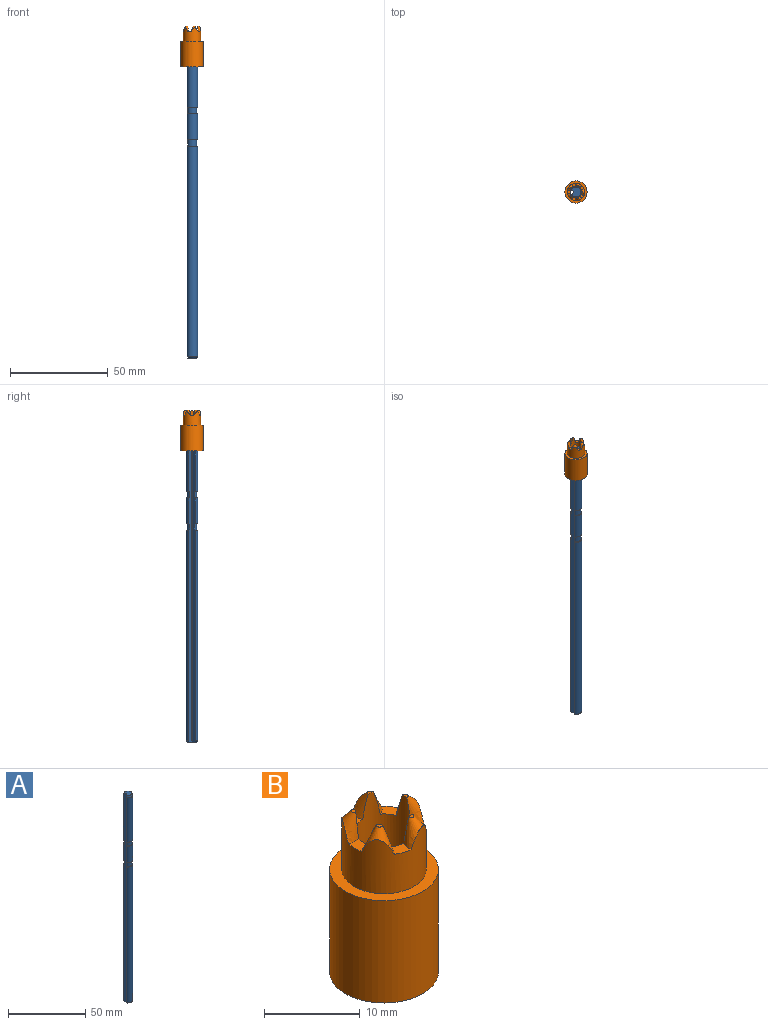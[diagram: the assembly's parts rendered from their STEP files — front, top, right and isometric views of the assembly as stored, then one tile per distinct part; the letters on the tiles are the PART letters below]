
ASSEMBLY  parts=2 mates=1
PART A: 16 faces, bbox 5.6x5.9x165 mm
  f0: cylinder r=2.95mm len=13.2mm, axis (0,0,-1), area 201.2mm2, adj f2,f4,f11,f15
  f1: cylinder r=2.95mm len=107.85mm, axis (0,0,-1), area 1643.7mm2, adj f2,f4,f8,f12
  f2: plane 165.02x1.36mm, normal (-0.71,0.71,0), area 307.8mm2, adj f0,f1,f3,f5,f6,f7,f8,f9
  f3: cylinder r=2.95mm len=35.25mm, axis (0,0,-1), area 537.2mm2, adj f2,f4,f9,f14
  f4: plane 165.02x1.36mm, normal (-0.71,-0.71,0), area 307.8mm2, adj f0,f1,f3,f5,f6,f7,f8,f9
  f5: cylinder r=0.3mm len=165mm, axis (0,0,-1), area 77.8mm2, adj f2,f4,f6,f7
  f6: plane 5.09x4.75mm, normal (0,0,1), area 18.2mm2, adj f2,f4,f5,f9
  f7: plane 4.69x4.41mm, normal (0,0,-1), area 15.6mm2, adj f2,f4,f5,f8
  f8: cone r=2.95mm half-angle=45deg, axis (0,0,1), area 11.7mm2, adj f1,f2,f4,f7
  f9: cone r=2.54mm half-angle=15deg, axis (0,0,-1), area 22.2mm2, adj f2,f3,f4,f6
  f10: cylinder r=2.4mm len=4.8mm, axis (0,0,-1), area 41.8mm2, adj f2,f4,f11,f12
  f11: plane 5.89x5.45mm, normal (0,0,-1), area 7.6mm2, adj f0,f2,f4,f10
  f12: plane 5.89x5.45mm, normal (0,0,1), area 7.6mm2, adj f1,f2,f4,f10
  f13: cylinder r=2.4mm len=4.8mm, axis (0,0,-1), area 41.8mm2, adj f2,f4,f14,f15
  f14: plane 5.89x5.45mm, normal (0,0,-1), area 7.6mm2, adj f2,f3,f4,f13
  f15: plane 5.89x5.45mm, normal (0,0,1), area 7.6mm2, adj f0,f2,f4,f13
PART B: 20 faces, bbox 11.7x11.7x21.3 mm
  f0: cone r=1.8mm half-angle=24.8deg, axis (0.34,0,-0.94), area 9.2mm2, adj f1,f2,f3,f4,f16
  f1: plane 0.98x0.75mm, normal (0,0,1), area 0.2mm2, adj f0,f2
  f2: cylinder r=3.04mm len=20.85mm, axis (0,0,-1), area 363.1mm2, adj f0,f1,f4,f5,f6,f7,f8,f9
  f3: cylinder r=4.4mm len=8.8mm, axis (0,0,-1), area 159.2mm2, adj f0,f4,f6,f7,f9,f10,f12,f13
  f4: plane 2.34x2.24mm, normal (0,0,1), area 2.3mm2, adj f0,f2,f3,f6
  f5: plane 0.98x0.84mm, normal (0,0,1), area 0.2mm2, adj f2,f6
  f6: cone r=1.8mm half-angle=24.8deg, axis (0.11,0.33,-0.94), area 9.2mm2, adj f2,f3,f4,f5,f7
  f7: plane 2.22x1.93mm, normal (0,0,1), area 2.3mm2, adj f2,f3,f6,f9
  f8: plane 0.96x0.91mm, normal (0,0,1), area 0.2mm2, adj f2,f9
  f9: cone r=1.8mm half-angle=24.8deg, axis (-0.28,0.2,-0.94), area 9.2mm2, adj f2,f3,f7,f8,f10
  f10: plane 2.02x1.55mm, normal (0,0,1), area 2.3mm2, adj f2,f3,f9,f12
  f11: plane 0.96x0.91mm, normal (0,0,1), area 0.2mm2, adj f2,f12
  f12: cone r=1.8mm half-angle=24.8deg, axis (-0.28,-0.2,-0.94), area 9.2mm2, adj f2,f3,f10,f11,f13
  f13: plane 2.22x1.93mm, normal (0,0,1), area 2.3mm2, adj f2,f3,f12,f14
  f14: cone r=1.8mm half-angle=24.8deg, axis (0.11,-0.33,-0.94), area 9.2mm2, adj f2,f3,f13,f15,f16
  f15: plane 0.98x0.84mm, normal (0,0,1), area 0.2mm2, adj f2,f14
  f16: plane 2.34x2.24mm, normal (0,0,1), area 2.3mm2, adj f0,f2,f3,f14
  f17: cylinder r=5.68mm len=13.05mm, axis (0,0,1), area 465.3mm2, adj f18,f19
  f18: plane 11.35x11.35mm, normal (0,0,-1), area 72.1mm2, adj f2,f17
  f19: plane 11.35x11.35mm, normal (0,0,1), area 40.4mm2, adj f3,f17
PLACE A t=(0,0,-162.15)mm
PLACE B at identity fixed
MATE fastened A.f0 <-> B.f2  axis (0,0,1) through (0,0,2.85)mm
